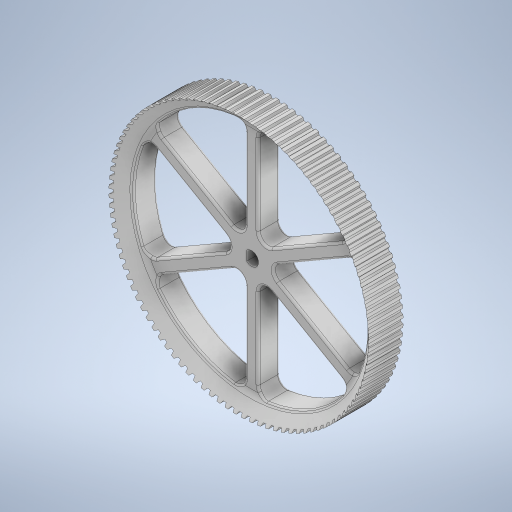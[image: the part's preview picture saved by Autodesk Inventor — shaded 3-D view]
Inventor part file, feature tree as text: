
AUTODESK INVENTOR PART (.ipt)
format: ipt  version: 2024.2 (Build 282272000, 272)  size: 1,231,360 bytes
history: native  units: mm
features: fillet x4, sketch x3, extrude x2, revolve x1, chamfer x1
ambient origin geometry x8: Origin, YZ Plane, XZ Plane, XY Plane, X Axis, Y Axis, Z Axis, Center Point
bodies: Solid1 (feature_tree)
feature tree (11):
  revolve  "Revolution1"  [1 undecoded]
  extrude  "Extrusion1"  Depth=30.0mm
  extrude  "Extrusion2"  Depth=0.5mm
  fillet  "Fillet1"  Radius=1.6mm
  fillet  "Fillet2"  Radius=1.0mm
  fillet  "Fillet3"  Radius=1000.0mm
  fillet  "Fillet4"  Radius=10.0mm
  chamfer  "Chamfer1"  Distance=3.2mm
  sketch  "Sketch1"  dims[d0=3.0mm d1=8.0mm]
  sketch  "Sketch2"  dims[d2=5.0mm d3=30.0mm]
  sketch  "Sketch3"  dims[d4=90.0deg d6=0.5mm d7=1.6mm d8=1.0mm d9=1000.0mm d11=360.0deg d13=10.0mm d14=0.0mm d15=3.2mm d16=2.75mm d17=7.0mm d18=3.0mm d19=1.5mm d20=60.0mm d22=360.0deg d24=5.0mm d25=0.0mm d26=2.0mm d27=2.0mm d28=0.5mm d29=0.5mm d30=0.4mm d31=2.0mm d32=45.0deg d33=120.0deg d34=120.0deg]
note: 1 required parameter value undecoded (feature->parameter linkage not recoverable at this tier; creation-order binding heuristic only, values carry confidence <= 0.55)
